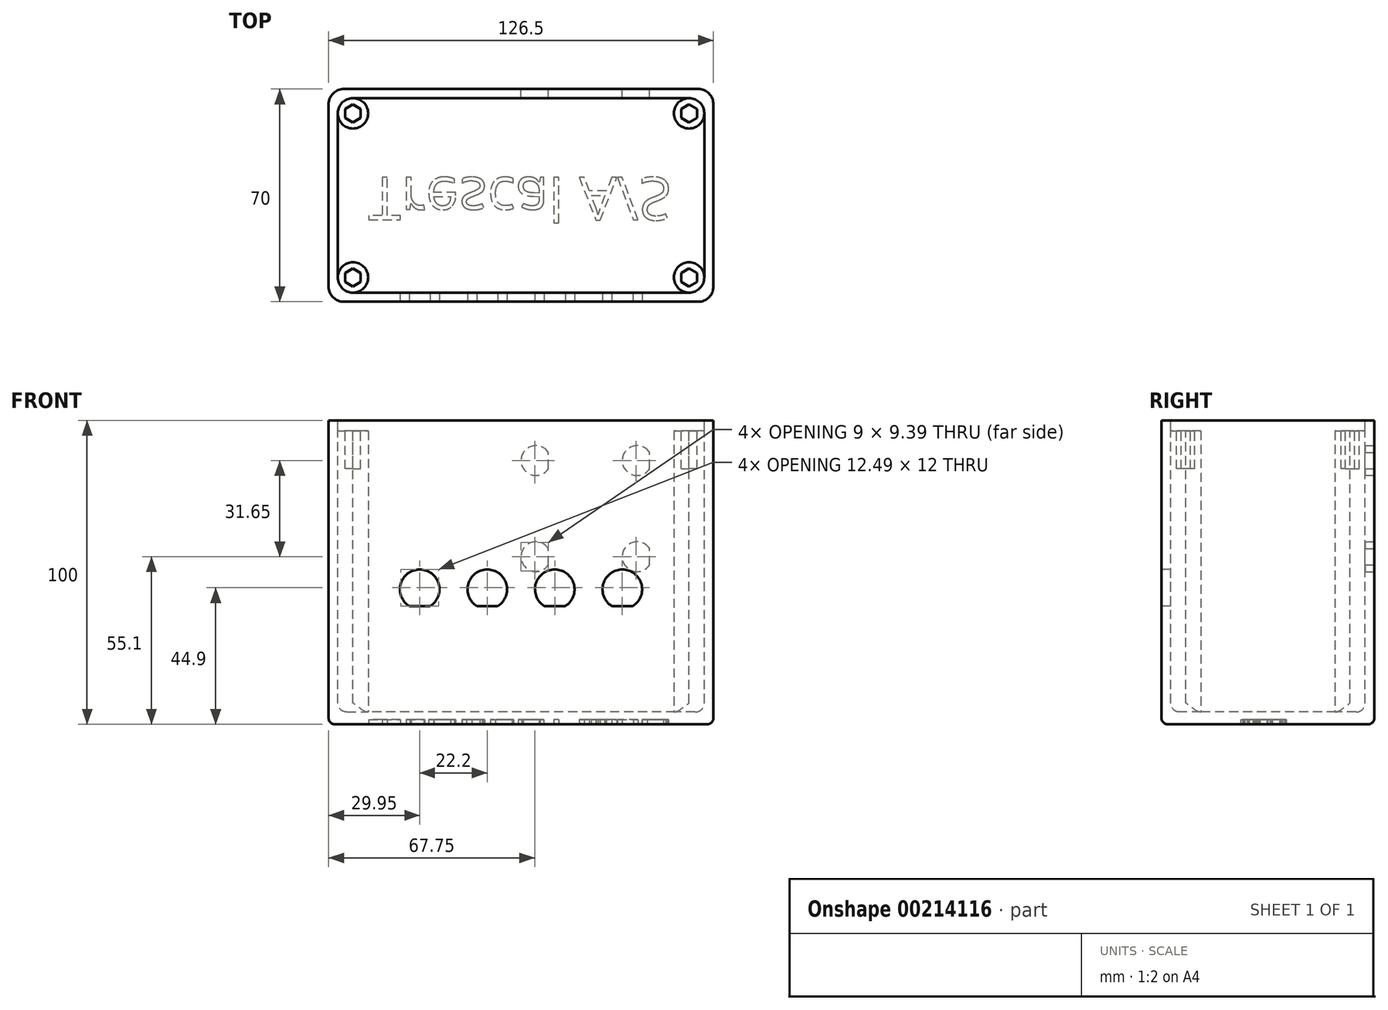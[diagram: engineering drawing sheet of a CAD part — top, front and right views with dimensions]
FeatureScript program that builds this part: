
annotation { "Feature Type Name" : "Feature", "Feature Type Description" : "" }
export const myFeature = defineFeature(function(context is Context, id is Id, definition is map)
    precondition{}
    {
        {
            var Q0;
            Q0=qCreatedBy(makeId("Top.planeOp"),FACE);
            var sketch = newSketch(context, id + "F0", { "sketchPlane" : qUnion([Q0])});
            skLineSegment(sketch, "E0.bottom", {"start": v(58.25, -35) * mm, "end": v(-58.25, -35) * mm});
            skLineSegment(sketch, "E0.top", {"start": v(58.25, 35) * mm, "end": v(-58.25, 35) * mm});
            skLineSegment(sketch, "E0.left", {"start": v(63.25, -30) * mm, "end": v(63.25, 30) * mm});
            skLineSegment(sketch, "E0.right", {"start": v(-63.25, -30) * mm, "end": v(-63.25, 30) * mm});
            skPoint(sketch, "E0.middle", {"position": v(0, 0) * mm});
            skPoint(sketch, "E1.visualSharp", {"position": v(-63.25, 35) * mm});
            skArc(sketch, "E1.filletArc", {"start": v(-58.25, 35) * mm, "mid": v(-61.79, 33.54) * mm, "end": v(-63.25, 30) * mm});
            skPoint(sketch, "E2.visualSharp", {"position": v(63.25, 35) * mm});
            skArc(sketch, "E2.filletArc", {"start": v(63.25, 30) * mm, "mid": v(61.79, 33.54) * mm, "end": v(58.25, 35) * mm});
            skPoint(sketch, "E3.visualSharp", {"position": v(63.25, -35) * mm});
            skArc(sketch, "E3.filletArc", {"start": v(58.25, -35) * mm, "mid": v(61.79, -33.54) * mm, "end": v(63.25, -30) * mm});
            skPoint(sketch, "E4.visualSharp", {"position": v(-63.25, -35) * mm});
            skArc(sketch, "E4.filletArc", {"start": v(-63.25, -30) * mm, "mid": v(-61.79, -33.54) * mm, "end": v(-58.25, -35) * mm});
            skSolve(sketch);
        }
        {
            var Q0;
            Q0=makeQuery(id+"F0.imprint","IMPRINT",FACE,{"disambiguationData":[TD([[makeQuery(id+"F0.imprint","IMPRINT",EDGE,{"derivedFrom":sQuery(id+"F0.wireOp",EDGE,"E0.bottom")}),-1.0]])]});
            extrude(context, id + "F1", {"entities" : qUnion([Q0]), "depth" : 100 * mm});
        }
        {
            var Q0;
            Q0=makeQuery(id+"F1.opExtrude","CAP_FACE",FACE,{"disambiguationData":[OSD([sQuery(id+"F0.wireOp",EDGE,"E0.bottom"),sQuery(id+"F0.wireOp",EDGE,"E0.top"),sQuery(id+"F0.wireOp",EDGE,"E0.left"),sQuery(id+"F0.wireOp",EDGE,"E0.right"),sQuery(id+"F0.wireOp",EDGE,"E1.filletArc"),sQuery(id+"F0.wireOp",EDGE,"E2.filletArc"),sQuery(id+"F0.wireOp",EDGE,"E3.filletArc"),sQuery(id+"F0.wireOp",EDGE,"E4.filletArc")])],"isStart":false});
            var sketch = newSketch(context, id + "F2", { "sketchPlane" : qUnion([Q0])});
            skLineSegment(sketch, "E5.bottom", {"start": v(55.25, 32) * mm, "end": v(-55.25, 32) * mm});
            skLineSegment(sketch, "E5.top", {"start": v(55.25, -32) * mm, "end": v(-55.25, -32) * mm});
            skLineSegment(sketch, "E5.left", {"start": v(60.25, 27) * mm, "end": v(60.25, -27) * mm});
            skLineSegment(sketch, "E5.right", {"start": v(-60.25, 27) * mm, "end": v(-60.25, -27) * mm});
            skPoint(sketch, "E5.middle", {"position": v(0, 0) * mm});
            skPoint(sketch, "E6.visualSharp", {"position": v(-60.25, 32) * mm});
            skArc(sketch, "E6.filletArc", {"start": v(-55.25, 32) * mm, "mid": v(-58.79, 30.54) * mm, "end": v(-60.25, 27) * mm});
            skPoint(sketch, "E7.visualSharp", {"position": v(60.25, 32) * mm});
            skArc(sketch, "E7.filletArc", {"start": v(60.25, 27) * mm, "mid": v(58.79, 30.54) * mm, "end": v(55.25, 32) * mm});
            skPoint(sketch, "E8.visualSharp", {"position": v(60.25, -32) * mm});
            skArc(sketch, "E8.filletArc", {"start": v(55.25, -32) * mm, "mid": v(58.79, -30.54) * mm, "end": v(60.25, -27) * mm});
            skPoint(sketch, "E9.visualSharp", {"position": v(-60.25, -32) * mm});
            skArc(sketch, "E9.filletArc", {"start": v(-60.25, -27) * mm, "mid": v(-58.79, -30.54) * mm, "end": v(-55.25, -32) * mm});
            skSolve(sketch);
        }
        {
            var Q0;
            Q0=makeQuery(id+"F2.imprint","IMPRINT",FACE,{"disambiguationData":[TD([[makeQuery(id+"F2.imprint","IMPRINT",EDGE,{"derivedFrom":sQuery(id+"F2.wireOp",EDGE,"E5.bottom")}),1.0]])]});
            extrude(context, id + "F3", {"entities" : qUnion([Q0]), "operationType" : NewBodyOperationType.REMOVE, "oppositeDirection" : true, "depth" : 96 * mm});
        }
        {
            var Q0;
            Q0=makeQuery(id+"F1.opExtrude","CAP_EDGE",EDGE,{"disambiguationData":[OSD([sQuery(id+"F0.wireOp",EDGE,"E0.left")])],"isStart":true});
            var Q1;
            Q1=makeQuery(id+"F1.opExtrude","CAP_EDGE",EDGE,{"disambiguationData":[OSD([sQuery(id+"F0.wireOp",EDGE,"E3.filletArc")])],"isStart":true});
            var Q2;
            Q2=makeQuery(id+"F1.opExtrude","CAP_EDGE",EDGE,{"disambiguationData":[OSD([sQuery(id+"F0.wireOp",EDGE,"E0.bottom")])],"isStart":true});
            var Q3;
            Q3=makeQuery(id+"F1.opExtrude","CAP_EDGE",EDGE,{"disambiguationData":[OSD([sQuery(id+"F0.wireOp",EDGE,"E2.filletArc")])],"isStart":true});
            var Q4;
            Q4=makeQuery(id+"F1.opExtrude","CAP_EDGE",EDGE,{"disambiguationData":[OSD([sQuery(id+"F0.wireOp",EDGE,"E0.top")])],"isStart":true});
            var Q5;
            Q5=makeQuery(id+"F1.opExtrude","CAP_EDGE",EDGE,{"disambiguationData":[OSD([sQuery(id+"F0.wireOp",EDGE,"E1.filletArc")])],"isStart":true});
            var Q6;
            Q6=makeQuery(id+"F1.opExtrude","CAP_EDGE",EDGE,{"disambiguationData":[OSD([sQuery(id+"F0.wireOp",EDGE,"E0.right")])],"isStart":true});
            var Q7;
            Q7=makeQuery(id+"F1.opExtrude","CAP_EDGE",EDGE,{"disambiguationData":[OSD([sQuery(id+"F0.wireOp",EDGE,"E4.filletArc")])],"isStart":true});
            fillet(context, id + "F4", {"entities" : qUnion([Q0, Q1, Q2, Q3, Q4, Q5, Q6, Q7]), "radius" : 2 * mm, "tangentPropagation" : true, "allowEdgeOverflow" : false});
        }
        {
            var Q0;
            Q0=makeQuery(id+"F3.boolean.opBoolean","COPY",FACE,{"derivedFrom":makeQuery(id+"F3.opExtrude","CAP_FACE",FACE,{"disambiguationData":[OSD([sQuery(id+"F2.wireOp",EDGE,"E5.bottom"),sQuery(id+"F2.wireOp",EDGE,"E5.top"),sQuery(id+"F2.wireOp",EDGE,"E5.left"),sQuery(id+"F2.wireOp",EDGE,"E5.right"),sQuery(id+"F2.wireOp",EDGE,"E6.filletArc"),sQuery(id+"F2.wireOp",EDGE,"E7.filletArc"),sQuery(id+"F2.wireOp",EDGE,"E8.filletArc"),sQuery(id+"F2.wireOp",EDGE,"E9.filletArc")])],"isStart":false})});
            var sketch = newSketch(context, id + "F5", { "sketchPlane" : qUnion([Q0])});
            skCircle(sketch, "E10", {"center": v(-55.25, 27) * mm, "radius": 5 * mm});
            skCircle(sketch, "E11.MirrorC", {"center": v(55.25, 27) * mm, "radius": 5 * mm});
            skCircle(sketch, "E12.MirrorC", {"center": v(-55.25, -27) * mm, "radius": 5 * mm});
            skCircle(sketch, "E13.MirrorC", {"center": v(55.25, -27) * mm, "radius": 5 * mm});
            skSolve(sketch);
        }
        {
            var Q0;
            Q0 = qSketchRegion(id + "F5", true);
            extrude(context, id + "F6", {"entities" : qUnion([Q0]), "operationType" : NewBodyOperationType.ADD, "depth" : 92.5 * mm});
        }
        {
            var Q0;
            Q0=makeQuery(id+"F6.opExtrude","CAP_FACE",FACE,{"disambiguationData":[OSD([sQuery(id+"F5.wireOp",EDGE,"E10")])],"isStart":false});
            var sketch = newSketch(context, id + "F7", { "sketchPlane" : qUnion([Q0])});
            skPoint(sketch, "E14", {"position": v(-55.25, 27) * mm});
            skCircle(sketch, "E15.cCircle", {"center": v(-55.25, 27) * mm, "radius": 2.58 * mm, "construction": true});
            skLineSegment(sketch, "E15.0", {"start": v(-52.67, 25.51) * mm, "end": v(-55.25, 24.02) * mm});
            skLineSegment(sketch, "E15.1", {"start": v(-55.25, 24.02) * mm, "end": v(-57.83, 25.51) * mm});
            skLineSegment(sketch, "E15.2", {"start": v(-57.83, 25.51) * mm, "end": v(-57.83, 28.49) * mm});
            skLineSegment(sketch, "E15.3", {"start": v(-57.83, 28.49) * mm, "end": v(-55.25, 29.98) * mm});
            skLineSegment(sketch, "E15.4", {"start": v(-55.25, 29.98) * mm, "end": v(-52.67, 28.49) * mm});
            skLineSegment(sketch, "E15.5", {"start": v(-52.67, 28.49) * mm, "end": v(-52.67, 25.51) * mm});
            skPoint(sketch, "E15.0.midPoint", {"position": v(-53.96, 24.77) * mm});
            skCircle(sketch, "E16.MirrorC", {"center": v(55.25, 27) * mm, "radius": 2.58 * mm, "construction": true});
            skPoint(sketch, "E17.MirrorP", {"position": v(53.96, 24.77) * mm});
            skLineSegment(sketch, "E18.MirrorCS", {"start": v(57.83, 28.49) * mm, "end": v(55.25, 29.98) * mm});
            skLineSegment(sketch, "E19.MirrorCS", {"start": v(55.25, 29.98) * mm, "end": v(52.67, 28.49) * mm});
            skLineSegment(sketch, "E20.MirrorCS", {"start": v(52.67, 28.49) * mm, "end": v(52.67, 25.51) * mm});
            skLineSegment(sketch, "E21.MirrorCS", {"start": v(52.67, 25.51) * mm, "end": v(55.25, 24.02) * mm});
            skLineSegment(sketch, "E22.MirrorCS", {"start": v(55.25, 24.02) * mm, "end": v(57.83, 25.51) * mm});
            skLineSegment(sketch, "E23.MirrorCS", {"start": v(57.83, 25.51) * mm, "end": v(57.83, 28.49) * mm});
            skLineSegment(sketch, "E24.MirrorCS", {"start": v(-57.83, -25.51) * mm, "end": v(-57.83, -28.49) * mm});
            skLineSegment(sketch, "E25.MirrorCS", {"start": v(-57.83, -28.49) * mm, "end": v(-55.25, -29.98) * mm});
            skLineSegment(sketch, "E26.MirrorCS", {"start": v(-55.25, -29.98) * mm, "end": v(-52.67, -28.49) * mm});
            skLineSegment(sketch, "E27.MirrorCS", {"start": v(-52.67, -28.49) * mm, "end": v(-52.67, -25.51) * mm});
            skLineSegment(sketch, "E28.MirrorCS", {"start": v(-52.67, -25.51) * mm, "end": v(-55.25, -24.02) * mm});
            skLineSegment(sketch, "E29.MirrorCS", {"start": v(-55.25, -24.02) * mm, "end": v(-57.83, -25.51) * mm});
            skCircle(sketch, "E30.MirrorC", {"center": v(-55.25, -27) * mm, "radius": 2.58 * mm, "construction": true});
            skLineSegment(sketch, "E31.MirrorCS", {"start": v(57.83, -28.49) * mm, "end": v(55.25, -29.98) * mm});
            skLineSegment(sketch, "E32.MirrorCS", {"start": v(57.83, -25.51) * mm, "end": v(57.83, -28.49) * mm});
            skLineSegment(sketch, "E33.MirrorCS", {"start": v(55.25, -24.02) * mm, "end": v(57.83, -25.51) * mm});
            skLineSegment(sketch, "E34.MirrorCS", {"start": v(52.67, -25.51) * mm, "end": v(55.25, -24.02) * mm});
            skLineSegment(sketch, "E35.MirrorCS", {"start": v(52.67, -28.49) * mm, "end": v(52.67, -25.51) * mm});
            skLineSegment(sketch, "E36.MirrorCS", {"start": v(55.25, -29.98) * mm, "end": v(52.67, -28.49) * mm});
            skCircle(sketch, "E37.MirrorC", {"center": v(55.25, -27) * mm, "radius": 2.58 * mm, "construction": true});
            skSolve(sketch);
        }
        {
            var Q0;
            Q0 = qSketchRegion(id + "F7", true);
            extrude(context, id + "F8", {"entities" : qUnion([Q0]), "operationType" : NewBodyOperationType.REMOVE, "oppositeDirection" : true, "depth" : 12.5 * mm});
        }
        {
            var Q0;
            Q0=makeQuery(id+"F1.opExtrude","CAP_FACE",FACE,{"disambiguationData":[OSD([sQuery(id+"F0.wireOp",EDGE,"E0.bottom"),sQuery(id+"F0.wireOp",EDGE,"E0.top"),sQuery(id+"F0.wireOp",EDGE,"E0.left"),sQuery(id+"F0.wireOp",EDGE,"E0.right"),sQuery(id+"F0.wireOp",EDGE,"E1.filletArc"),sQuery(id+"F0.wireOp",EDGE,"E2.filletArc"),sQuery(id+"F0.wireOp",EDGE,"E3.filletArc"),sQuery(id+"F0.wireOp",EDGE,"E4.filletArc")])],"isStart":true});
            var sketch = newSketch(context, id + "F9", { "sketchPlane" : qUnion([Q0])});
            skText(sketch, "E38", { "text": "Trescal A/S", "fontName": "OpenSans-Regular.ttf"});
            const initialGuessF9  = {"E38": [-0.05024, -0.00589, 1, 0, 0.01409]};
            skSetInitialGuess(sketch, initialGuessF9);
            skSolve(sketch);
        }
        {
            var Q0;
            Q0 = qSketchRegion(id + "F9", true);
            extrude(context, id + "F10", {"entities" : qUnion([Q0]), "operationType" : NewBodyOperationType.REMOVE, "oppositeDirection" : true, "depth" : 1.5 * mm});
        }
        {
            var Q0;
            Q0=makeQuery(id+"F1.opExtrude","SWEPT_FACE",FACE,{"disambiguationData":[OSD([sQuery(id+"F0.wireOp",EDGE,"E0.bottom")])]});
            var sketch = newSketch(context, id + "F11", { "sketchPlane" : qUnion([Q0])});
            skArc(sketch, "E39", {"start": v(-29.84, 38.9) * mm, "mid": v(-33.3, 50.9) * mm, "end": v(-36.76, 38.9) * mm});
            skLineSegment(sketch, "E40", {"start": v(-29.84, 38.9) * mm, "end": v(-36.76, 38.9) * mm});
            skArc(sketch, "E41", {"start": v(-7.64, 38.9) * mm, "mid": v(-11.1, 50.9) * mm, "end": v(-14.56, 38.9) * mm});
            skLineSegment(sketch, "E42", {"start": v(-7.64, 38.9) * mm, "end": v(-14.56, 38.9) * mm});
            skArc(sketch, "E43.MirrorCS", {"start": v(29.84, 38.9) * mm, "mid": v(33.3, 50.9) * mm, "end": v(36.76, 38.9) * mm});
            skLineSegment(sketch, "E44.MirrorCS", {"start": v(7.64, 38.9) * mm, "end": v(14.56, 38.9) * mm});
            skLineSegment(sketch, "E45.MirrorCS", {"start": v(29.84, 38.9) * mm, "end": v(36.76, 38.9) * mm});
            skArc(sketch, "E46.MirrorCS", {"start": v(7.64, 38.9) * mm, "mid": v(11.1, 50.9) * mm, "end": v(14.56, 38.9) * mm});
            skSolve(sketch);
        }
        {
            var Q0;
            Q0 = qSketchRegion(id + "F11", true);
            extrude(context, id + "F12", {"entities" : qUnion([Q0]), "operationType" : NewBodyOperationType.REMOVE, "oppositeDirection" : true, "depth" : 25 * mm});
        }
        {
            var Q0;
            Q0=makeQuery(id+"F1.opExtrude","SWEPT_FACE",FACE,{"disambiguationData":[OSD([sQuery(id+"F0.wireOp",EDGE,"E0.top")])]});
            var sketch = newSketch(context, id + "F13", { "sketchPlane" : qUnion([Q0])});
            skArc(sketch, "E47", {"start": v(-42.25, 84.07) * mm, "mid": v(-33.25, 86.75) * mm, "end": v(-42.25, 89.43) * mm});
            skLineSegment(sketch, "E48", {"start": v(-42.25, 84.07) * mm, "end": v(-42.25, 89.43) * mm});
            skArc(sketch, "E49", {"start": v(-42.25, 52.42) * mm, "mid": v(-33.25, 55.1) * mm, "end": v(-42.25, 57.78) * mm});
            skLineSegment(sketch, "E50", {"start": v(-42.25, 52.42) * mm, "end": v(-42.25, 57.78) * mm});
            skArc(sketch, "E51", {"start": v(-9, 52.42) * mm, "mid": v(0, 55.1) * mm, "end": v(-9, 57.78) * mm});
            skLineSegment(sketch, "E52", {"start": v(-9, 52.42) * mm, "end": v(-9, 57.78) * mm});
            skArc(sketch, "E53", {"start": v(-9, 84.07) * mm, "mid": v(0, 86.75) * mm, "end": v(-9, 89.43) * mm});
            skLineSegment(sketch, "E54", {"start": v(-9, 84.07) * mm, "end": v(-9, 89.43) * mm});
            skSolve(sketch);
        }
        {
            var Q0;
            Q0 = qSketchRegion(id + "F13", true);
            extrude(context, id + "F14", {"entities" : qUnion([Q0]), "operationType" : NewBodyOperationType.REMOVE, "oppositeDirection" : true, "depth" : 25 * mm});
        }
        {
            var Q0;
            Q0=makeQuery(id+"F3.boolean.opBoolean","COPY",EDGE,{"derivedFrom":makeQuery(id+"F3.opExtrude","CAP_EDGE",EDGE,{"disambiguationData":[OSD([sQuery(id+"F2.wireOp",EDGE,"E5.bottom")])],"isStart":false})});
            var Q1;
            Q1=makeQuery(id+"F6.opExtrude","CAP_EDGE",EDGE,{"disambiguationData":[OSD([sQuery(id+"F5.wireOp",EDGE,"E10")])],"isStart":true});
            var Q2;
            Q2=makeQuery(id+"F3.boolean.opBoolean","COPY",EDGE,{"derivedFrom":makeQuery(id+"F3.opExtrude","CAP_EDGE",EDGE,{"disambiguationData":[OSD([sQuery(id+"F2.wireOp",EDGE,"E5.right")])],"isStart":false})});
            var Q3;
            Q3=makeQuery(id+"F3.boolean.opBoolean","COPY",EDGE,{"derivedFrom":makeQuery(id+"F3.opExtrude","CAP_EDGE",EDGE,{"disambiguationData":[OSD([sQuery(id+"F2.wireOp",EDGE,"E5.top")])],"isStart":false})});
            var Q4;
            Q4=makeQuery(id+"F6.opExtrude","CAP_EDGE",EDGE,{"disambiguationData":[OSD([sQuery(id+"F5.wireOp",EDGE,"E13.MirrorC")])],"isStart":true});
            var Q5;
            Q5=makeQuery(id+"F3.boolean.opBoolean","COPY",EDGE,{"derivedFrom":makeQuery(id+"F3.opExtrude","CAP_EDGE",EDGE,{"disambiguationData":[OSD([sQuery(id+"F2.wireOp",EDGE,"E5.left")])],"isStart":false})});
            var Q6;
            Q6=makeQuery(id+"F6.opExtrude","CAP_EDGE",EDGE,{"disambiguationData":[OSD([sQuery(id+"F5.wireOp",EDGE,"E12.MirrorC")])],"isStart":true});
            var Q7;
            Q7=makeQuery(id+"F6.opExtrude","CAP_EDGE",EDGE,{"disambiguationData":[OSD([sQuery(id+"F5.wireOp",EDGE,"E11.MirrorC")])],"isStart":true});
            fillet(context, id + "F15", {"entities" : qUnion([Q0, Q1, Q2, Q3, Q4, Q5, Q6, Q7]), "radius" : 3 * mm, "tangentPropagation" : true, "allowEdgeOverflow" : false});
        }
    });
